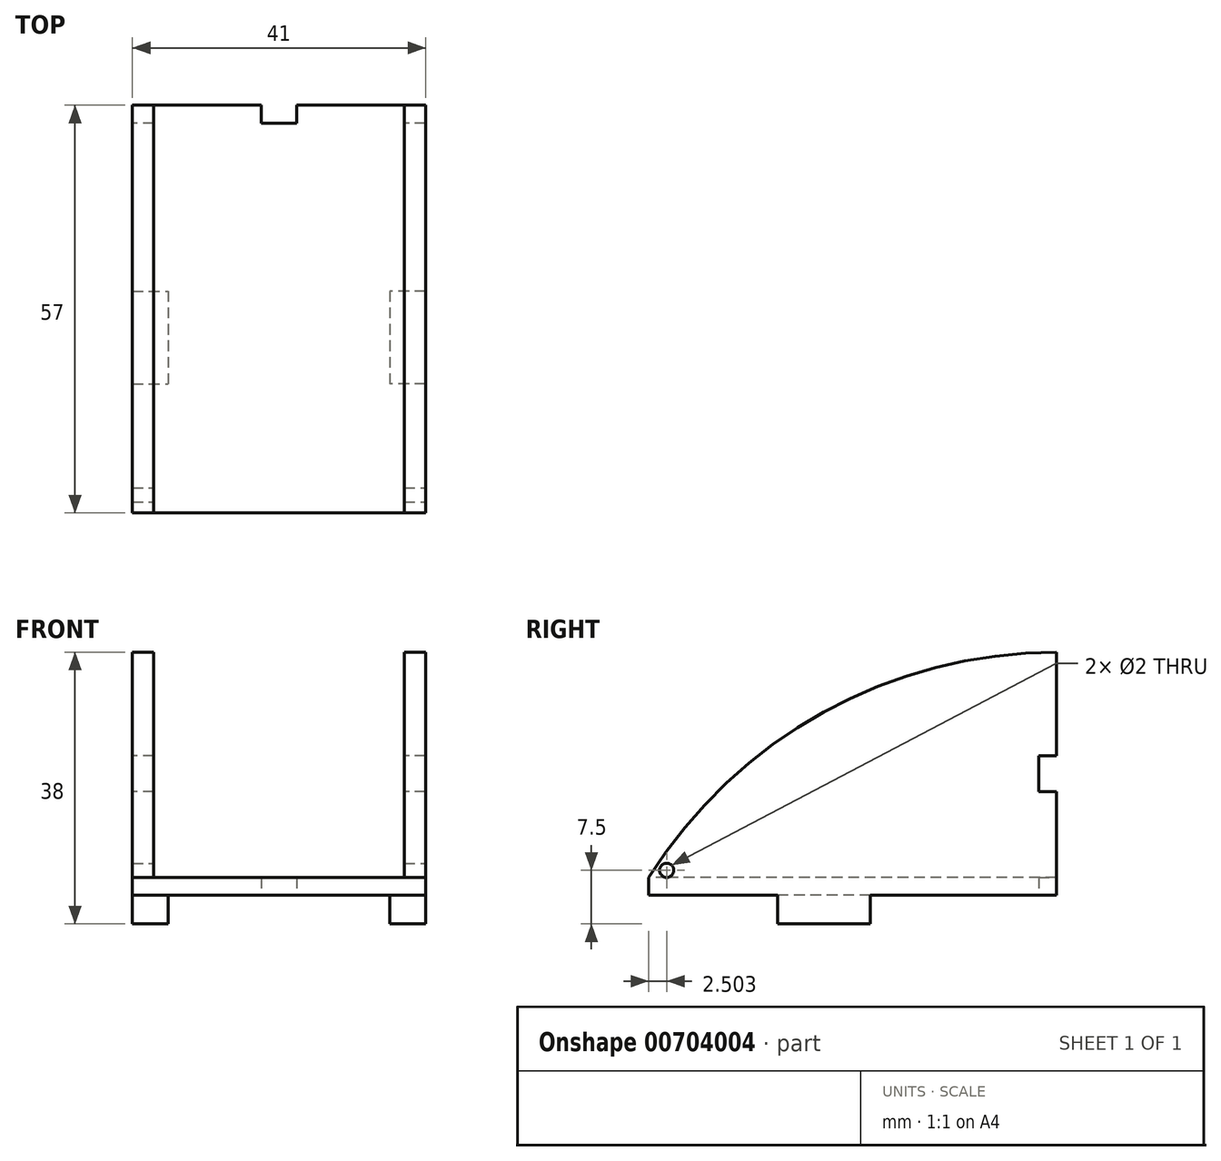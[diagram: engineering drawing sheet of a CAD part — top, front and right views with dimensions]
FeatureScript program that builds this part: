
annotation { "Feature Type Name" : "Feature", "Feature Type Description" : "" }
export const myFeature = defineFeature(function(context is Context, id is Id, definition is map)
    precondition{}
    {
        {
            var Q0;
            Q0=qCreatedBy(makeId("Top.planeOp"),FACE);
            var sketch = newSketch(context, id + "F0", { "sketchPlane" : qUnion([Q0])});
            skLineSegment(sketch, "E0.bottom", {"start": v(-23.81, 34.34) * mm, "end": v(17.19, 34.34) * mm});
            skLineSegment(sketch, "E0.top", {"start": v(-23.81, -22.66) * mm, "end": v(17.19, -22.66) * mm});
            skLineSegment(sketch, "E0.left", {"start": v(-23.81, 34.34) * mm, "end": v(-23.81, -22.66) * mm});
            skLineSegment(sketch, "E0.right", {"start": v(17.19, 34.34) * mm, "end": v(17.19, -22.66) * mm});
            skSolve(sketch);
        }
        {
            var Q0;
            Q0=makeQuery(id+"F0.imprint","IMPRINT",FACE,{"disambiguationData":[TD([[makeQuery(id+"F0.imprint","IMPRINT",EDGE,{"derivedFrom":sQuery(id+"F0.wireOp",EDGE,"E0.bottom")}),-1.0]])]});
            extrude(context, id + "F1", {"entities" : qUnion([Q0]), "depth" : 34 * mm, "offsetDistance" : 25 * mm});
        }
        {
            var Q0;
            Q0=makeQuery(id+"F1.opExtrude","CAP_FACE",FACE,{"disambiguationData":[OSD([sQuery(id+"F0.wireOp",EDGE,"E0.bottom"),sQuery(id+"F0.wireOp",EDGE,"E0.top"),sQuery(id+"F0.wireOp",EDGE,"E0.left"),sQuery(id+"F0.wireOp",EDGE,"E0.right")])],"isStart":false});
            var sketch = newSketch(context, id + "F2", { "sketchPlane" : qUnion([Q0])});
            skLineSegment(sketch, "E1.bottom", {"start": v(-20.81, 34.34) * mm, "end": v(14.19, 34.34) * mm});
            skLineSegment(sketch, "E1.top", {"start": v(-20.81, -22.66) * mm, "end": v(14.19, -22.66) * mm});
            skLineSegment(sketch, "E1.left", {"start": v(-20.81, 34.34) * mm, "end": v(-20.81, -22.66) * mm});
            skLineSegment(sketch, "E1.right", {"start": v(14.19, 34.34) * mm, "end": v(14.19, -22.66) * mm});
            skSolve(sketch);
        }
        {
            var Q0;
            Q0=makeQuery(id+"F2.imprint","IMPRINT",FACE,{"disambiguationData":[TD([[makeQuery(id+"F2.imprint","IMPRINT",EDGE,{"derivedFrom":sQuery(id+"F2.wireOp",EDGE,"E1.bottom")}),-1.0]])]});
            extrude(context, id + "F3", {"entities" : qUnion([Q0]), "operationType" : NewBodyOperationType.REMOVE, "oppositeDirection" : true, "depth" : 31.5 * mm, "offsetDistance" : 25 * mm});
        }
        {
            var Q0;
            Q0=makeQuery(id+"F1.opExtrude","SWEPT_FACE",FACE,{"disambiguationData":[OSD([sQuery(id+"F0.wireOp",EDGE,"E0.right")])]});
            var sketch = newSketch(context, id + "F4", { "sketchPlane" : qUnion([Q0])});
            skArc(sketch, "E2", {"start": v(34.34, 34) * mm, "mid": v(1.78, 25.6) * mm, "end": v(-22.66, 2.5) * mm});
            skLineSegment(sketch, "E3", {"start": v(-22.66, 2.5) * mm, "end": v(34.34, 2.5) * mm});
            skLineSegment(sketch, "E4", {"start": v(34.34, 2.5) * mm, "end": v(34.34, 34) * mm});
            skSolve(sketch);
        }
        {
            var Q0;
            {var subQ0=sQuery(id+"F4.wireOp",EDGE,"E2");Q0=makeQuery(id+"F4.imprint","IMPRINT",FACE,{"disambiguationData":[TD([[makeQuery(id+"F4.imprint","IMPRINT",EDGE,{"derivedFrom":subQ0}),-1.0]])]});}
            extrude(context, id + "F5", {"entities" : qUnion([Q0]), "operationType" : NewBodyOperationType.REMOVE, "endBound" : BoundingType.THROUGH_ALL, "oppositeDirection" : true, "depth" : 25 * mm, "offsetDistance" : 25 * mm});
        }
        {
            var Q0;
            Q0=makeQuery(id+"F1.opExtrude","SWEPT_FACE",FACE,{"disambiguationData":[OSD([sQuery(id+"F0.wireOp",EDGE,"E0.right")])]});
            var sketch = newSketch(context, id + "F6", { "sketchPlane" : qUnion([Q0])});
            skCircle(sketch, "E5", {"center": v(-20.16, 3.5) * mm, "radius": 1 * mm});
            skSolve(sketch);
        }
        {
            var Q0;
            Q0=makeQuery(id+"F6.imprint","IMPRINT",FACE,{"disambiguationData":[TD([[makeQuery(id+"F6.imprint","IMPRINT",EDGE,{"derivedFrom":sQuery(id+"F6.wireOp",EDGE,"E5")}),1.0]])]});
            extrude(context, id + "F7", {"entities" : qUnion([Q0]), "operationType" : NewBodyOperationType.REMOVE, "endBound" : BoundingType.THROUGH_ALL, "oppositeDirection" : true, "depth" : 25 * mm, "offsetDistance" : 25 * mm});
        }
        {
            var Q0;
            Q0=makeQuery(id+"F1.opExtrude","SWEPT_FACE",FACE,{"disambiguationData":[OSD([sQuery(id+"F0.wireOp",EDGE,"E0.bottom")])]});
            var sketch = newSketch(context, id + "F8", { "sketchPlane" : qUnion([Q0])});
            skLineSegment(sketch, "E6.bottom", {"start": v(5.81, 2.5) * mm, "end": v(0.81, 2.5) * mm});
            skLineSegment(sketch, "E6.top", {"start": v(5.81, 0) * mm, "end": v(0.81, 0) * mm});
            skLineSegment(sketch, "E6.left", {"start": v(5.81, 2.5) * mm, "end": v(5.81, 0) * mm});
            skLineSegment(sketch, "E6.right", {"start": v(0.81, 2.5) * mm, "end": v(0.81, 0) * mm});
            skLineSegment(sketch, "E7.bottom", {"start": v(20.81, 19.5) * mm, "end": v(23.81, 19.5) * mm});
            skLineSegment(sketch, "E7.top", {"start": v(20.81, 14.5) * mm, "end": v(23.81, 14.5) * mm});
            skLineSegment(sketch, "E7.left", {"start": v(20.81, 19.5) * mm, "end": v(20.81, 14.5) * mm});
            skLineSegment(sketch, "E7.right", {"start": v(23.81, 19.5) * mm, "end": v(23.81, 14.5) * mm});
            skLineSegment(sketch, "E8.bottom", {"start": v(-17.19, 19.5) * mm, "end": v(-14.19, 19.5) * mm});
            skLineSegment(sketch, "E8.top", {"start": v(-17.19, 14.5) * mm, "end": v(-14.19, 14.5) * mm});
            skLineSegment(sketch, "E8.left", {"start": v(-17.19, 19.5) * mm, "end": v(-17.19, 14.5) * mm});
            skLineSegment(sketch, "E8.right", {"start": v(-14.19, 19.5) * mm, "end": v(-14.19, 14.5) * mm});
            skSolve(sketch);
        }
        {
            var Q0;
            Q0=makeQuery(id+"F8.imprint","IMPRINT",FACE,{"disambiguationData":[TD([[makeQuery(id+"F8.imprint","IMPRINT",EDGE,{"derivedFrom":sQuery(id+"F8.wireOp",EDGE,"E8.bottom")}),-1.0]])]});
            var Q1;
            Q1=makeQuery(id+"F8.imprint","IMPRINT",FACE,{"disambiguationData":[TD([[makeQuery(id+"F8.imprint","IMPRINT",EDGE,{"derivedFrom":sQuery(id+"F8.wireOp",EDGE,"E6.bottom")}),1.0]])]});
            var Q2;
            Q2=makeQuery(id+"F8.imprint","IMPRINT",FACE,{"disambiguationData":[TD([[makeQuery(id+"F8.imprint","IMPRINT",EDGE,{"derivedFrom":sQuery(id+"F8.wireOp",EDGE,"E7.bottom")}),-1.0]])]});
            extrude(context, id + "F9", {"entities" : qUnion([Q0, Q1, Q2]), "operationType" : NewBodyOperationType.REMOVE, "oppositeDirection" : true, "depth" : 2.5 * mm, "offsetDistance" : 25 * mm});
        }
        {
            var Q0;
            Q0=makeQuery(id+"F1.opExtrude","CAP_FACE",FACE,{"disambiguationData":[OSD([sQuery(id+"F0.wireOp",EDGE,"E0.bottom"),sQuery(id+"F0.wireOp",EDGE,"E0.top"),sQuery(id+"F0.wireOp",EDGE,"E0.left"),sQuery(id+"F0.wireOp",EDGE,"E0.right")])],"isStart":true});
            var sketch = newSketch(context, id + "F10", { "sketchPlane" : qUnion([Q0])});
            skLineSegment(sketch, "E9.bottom", {"start": v(17.19, -8.34) * mm, "end": v(12.19, -8.34) * mm});
            skLineSegment(sketch, "E9.top", {"start": v(17.19, 4.66) * mm, "end": v(12.19, 4.66) * mm});
            skLineSegment(sketch, "E9.left", {"start": v(17.19, -8.34) * mm, "end": v(17.19, 4.66) * mm});
            skLineSegment(sketch, "E9.right", {"start": v(12.19, -8.34) * mm, "end": v(12.19, 4.66) * mm});
            skLineSegment(sketch, "E10.bottom", {"start": v(-23.81, -8.34) * mm, "end": v(-18.81, -8.34) * mm});
            skLineSegment(sketch, "E10.top", {"start": v(-23.81, 4.66) * mm, "end": v(-18.81, 4.66) * mm});
            skLineSegment(sketch, "E10.left", {"start": v(-23.81, -8.34) * mm, "end": v(-23.81, 4.66) * mm});
            skLineSegment(sketch, "E10.right", {"start": v(-18.81, -8.34) * mm, "end": v(-18.81, 4.66) * mm});
            skSolve(sketch);
        }
        {
            var Q0;
            Q0=makeQuery(id+"F10.imprint","IMPRINT",FACE,{"disambiguationData":[TD([[makeQuery(id+"F10.imprint","IMPRINT",EDGE,{"derivedFrom":sQuery(id+"F10.wireOp",EDGE,"E9.bottom")}),-1.0]])]});
            var Q1;
            Q1=makeQuery(id+"F10.imprint","IMPRINT",FACE,{"disambiguationData":[TD([[makeQuery(id+"F10.imprint","IMPRINT",EDGE,{"derivedFrom":sQuery(id+"F10.wireOp",EDGE,"E10.bottom")}),1.0]])]});
            extrude(context, id + "F11", {"entities" : qUnion([Q0, Q1]), "operationType" : NewBodyOperationType.ADD, "depth" : 4 * mm, "offsetDistance" : 25 * mm});
        }
    });
